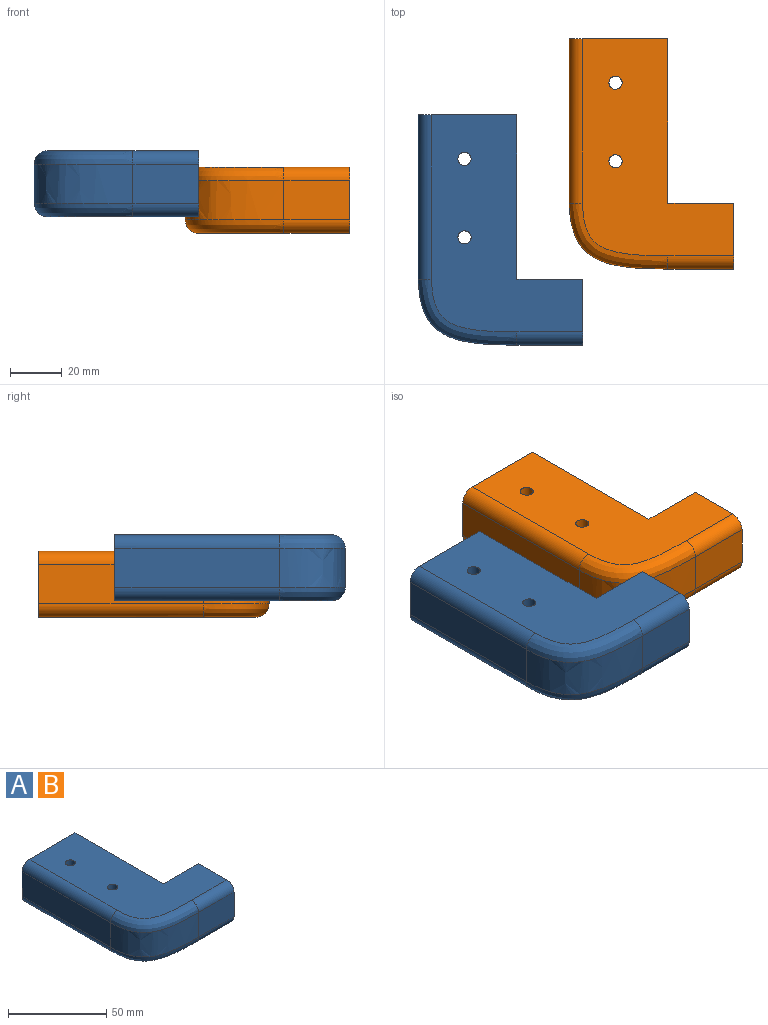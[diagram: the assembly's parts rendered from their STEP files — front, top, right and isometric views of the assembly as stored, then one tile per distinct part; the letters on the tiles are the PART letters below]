
ASSEMBLY  parts=2 mates=1
PART A: 17 faces, bbox 63.5x88.9x25.4 mm
  f0: plane 63.5x25.4mm, normal (1,0,0), area 1612.9mm2, adj f1,f8,f9,f10
  f1: plane 38.1x25.4mm, normal (0,1,0), area 956.7mm2, adj f0,f2,f9,f10,f11,f14
  f2: plane 63.5x15.24mm, normal (-1,0,0), area 967.7mm2, adj f1,f3,f11,f14
  f3: extruded ~38.1x25.4mm, area 813.5mm2, adj f2,f4,f12,f15
  f4: plane 25.4x15.24mm, normal (0,-1,0), area 387.1mm2, adj f3,f5,f13,f16
  f5: plane 25.4x25.4mm, normal (1,0,0), area 634.1mm2, adj f4,f8,f9,f10,f13,f16
  f6: cylinder r=2.54mm len=25.4mm, axis (0,0,-1), area 405.4mm2, adj f9,f10
  f7: cylinder r=2.54mm len=25.4mm, axis (0,0,-1), area 405.4mm2, adj f9,f10
  f8: plane 25.4x25.4mm, normal (0,1,0), area 645.2mm2, adj f0,f5,f9,f10
  f9: plane 83.82x58.43mm, normal (0,0,1), area 3165.2mm2, adj f0,f1,f5,f6,f7,f8,f14,f15
  f10: plane 83.82x58.42mm, normal (0,0,-1), area 3165.2mm2, adj f0,f1,f5,f6,f7,f8,f11,f12
  f11: cylinder r=5.08mm len=63.5mm, axis (0,-1,0), area 506.5mm2, adj f1,f2,f10,f12
  f12: bspline ~54.83x26.1mm, area 402.9mm2, adj f3,f10,f11,f13
  f13: cylinder r=5.08mm len=25.4mm, axis (1,0,0), area 202.7mm2, adj f4,f5,f10,f12
  f14: cylinder r=5.08mm len=63.5mm, axis (0,1,0), area 506.5mm2, adj f1,f2,f9,f15
  f15: bspline ~54.83x26.1mm, area 402.9mm2, adj f3,f9,f14,f16
  f16: cylinder r=5.08mm len=25.4mm, axis (-1,0,0), area 202.7mm2, adj f4,f5,f9,f15
PART B: same geometry as A
PLACE A t=(-34.54,-26.68,11.27)mm
PLACE B t=(23.74,2.72,4.9)mm
MATE parallel A.f5 <-> B.f5  axis (1,0,0) through (-9.14,-39.18,23.97)mm
